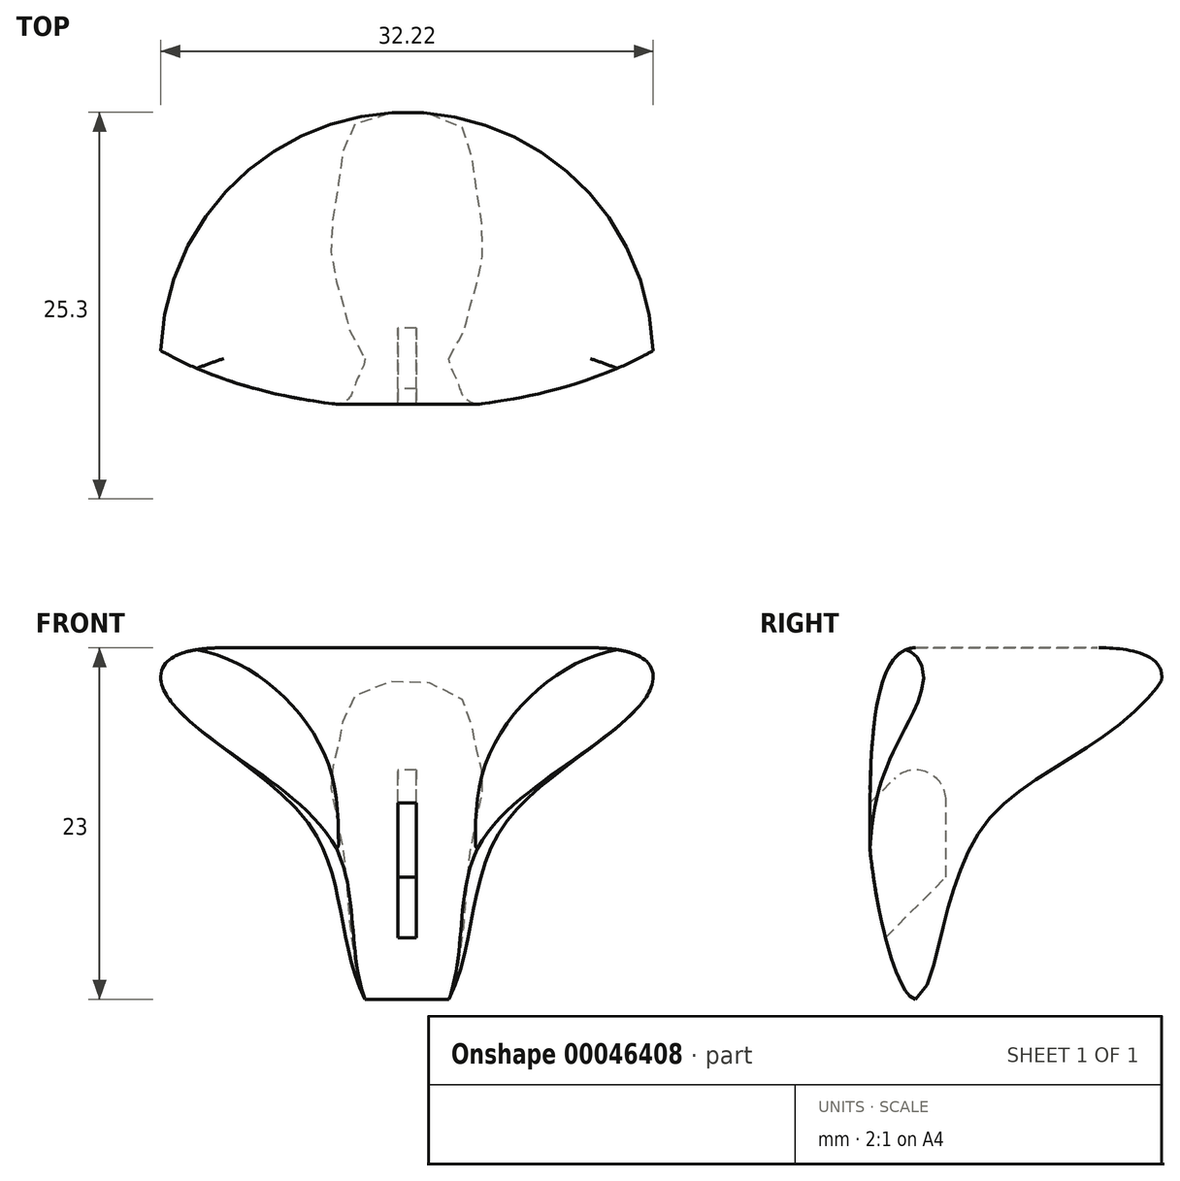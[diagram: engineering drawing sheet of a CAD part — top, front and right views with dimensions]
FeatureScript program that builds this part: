
annotation { "Feature Type Name" : "Feature", "Feature Type Description" : "" }
export const myFeature = defineFeature(function(context is Context, id is Id, definition is map)
    precondition{}
    {
        {
            var Q0;
            Q0=qCreatedBy(makeId("Front.planeOp"),FACE);
            var sketch = newSketch(context, id + "F0", { "sketchPlane" : qUnion([Q0])});
            skLineSegment(sketch, "E0", {"start": v(0, 15) * mm, "end": v(12, 15) * mm});
            skFitSpline(sketch, "E1", {"points": [v(12, 15) * mm, v(15.8, 12) * mm, v(7, 4.23) * mm, v(4, -3.98) * mm, v(0, -10) * mm], "startDerivative": vector(61.5, 0) * mm, "endDerivative": vector(-31.43, 0) * mm});
            skFitSpline(sketch, "E2.MirrorCS", {"points": [v(-12, 15) * mm, v(-15.8, 12) * mm, v(-7, 4.23) * mm, v(-4, -3.98) * mm, v(0, -10) * mm], "startDerivative": vector(-61.5, 0) * mm, "endDerivative": vector(31.43, 0) * mm});
            skLineSegment(sketch, "E3.MirrorCS", {"start": v(0, 15) * mm, "end": v(-12, 15) * mm});
            skLineSegment(sketch, "E4", {"start": v(0, 15) * mm, "end": v(0, -10) * mm});
            skSolve(sketch);
        }
        {
            var Q0;
            Q0=qCreatedBy(makeId("Right.planeOp"),FACE);
            var sketch = newSketch(context, id + "F1", { "sketchPlane" : qUnion([Q0])});
            skLineSegment(sketch, "E5", {"start": v(0, 15) * mm, "end": v(15, 15) * mm});
            skFitSpline(sketch, "E6", {"points": [v(15, 15) * mm, v(14.5, 11) * mm, v(5, 4) * mm, v(1.5, -4.5) * mm, v(0, -8) * mm, v(-3, 2) * mm, v(0, 15) * mm], "startDerivative": vector(73.61, 0) * mm, "endDerivative": vector(42.65, 0) * mm});
            skLineSegment(sketch, "E7", {"start": v(0, 15) * mm, "end": v(0, -8) * mm});
            skFitSpline(sketch, "E8", {"points": [v(0, 15) * mm, v(-3, 2) * mm], "startDerivative": vector(-9, 0) * mm, "endDerivative": vector(0, -17.41) * mm});
            skLineSegment(sketch, "E9", {"start": v(-3, 2) * mm, "end": v(-3, -8) * mm});
            skLineSegment(sketch, "E10", {"start": v(-3, -8) * mm, "end": v(0, -8) * mm});
            skSolve(sketch);
        }
        {
            var Q0;
            {var subQ0=sQuery(id+"F1.wireOp",EDGE,"8db3f753-8a20-43be-9b9b-d89ddbdbede4");Q0=makeQuery(id+"F1.imprint","IMPRINT",FACE,{"disambiguationData":[TD([[makeQuery(id+"F1.imprint","IMPRINT",EDGE,{"derivedFrom":subQ0}),-1.0]])]});}
            var Q1;
            {var subQ0=sQuery(id+"F1.wireOp",EDGE,"E5");Q1=makeQuery(id+"F1.imprint","IMPRINT",FACE,{"disambiguationData":[TD([[makeQuery(id+"F1.imprint","IMPRINT",EDGE,{"derivedFrom":subQ0}),-1.0]])]});}
            var Q2;
            Q2=makeQuery(id+"F1.imprint","IMPRINT",FACE,{"disambiguationData":[TD([[makeQuery(id+"F1.imprint","IMPRINT",EDGE,{"derivedFrom":sQuery(id+"F1.wireOp",EDGE,"E7")}),-1.0]])]});
            extrude(context, id + "F2", {"entities" : qUnion([Q0, Q1, Q2]), "depth" : 35 * mm, "offsetDistance" : 25 * mm, "symmetric" : true});
        }
        {
            var Q0;
            Q0=makeQuery(id+"F2.opExtrude","SWEPT_EDGE",EDGE,{"disambiguationData":[OSD([sQuery(id+"F1.wireOp",EDGE,"E9"),sQuery(id+"F1.wireOp",EDGE,"E10")])]});
            fillet(context, id + "F3", {"entities" : qUnion([Q0]), "tangentPropagation" : true, "radius" : 2 * mm, "defaultsChanged" : true, "vertexSettings" : [], "allowEdgeOverflow" : false});
        }
        {
            var Q0;
            Q0=makeQuery(id+"F0.imprint","IMPRINT",FACE,{"disambiguationData":[TD([[makeQuery(id+"F0.imprint","IMPRINT",EDGE,{"derivedFrom":sQuery(id+"F0.wireOp",EDGE,"E0")}),-1.0]])]});
            var Q1;
            Q1=sQuery(id+"F0.wireOp",EDGE,"E4");
            revolve(context, id + "F4", {"surfaceOperationType" : NewSurfaceOperationType.NEW, "entities" : qUnion([Q0]), "axis" : qUnion([Q1]), "revolveType" : RevolveType.FULL});
        }
        {
            var Q0;
            Q0=makeQuery(id+"F4.opRevolve","SWEPT_BODY",BODY,{"disambiguationData":[OSD([sQuery(id+"F0.wireOp",EDGE,"E0"),sQuery(id+"F0.wireOp",EDGE,"E1"),sQuery(id+"F0.wireOp",EDGE,"E4")])]});
            var Q1;
            Q1=makeQuery(id+"F2.opExtrude","SWEPT_BODY",BODY,{"disambiguationData":[OSD([sQuery(id+"F1.wireOp",EDGE,"E6"),sQuery(id+"F1.wireOp",EDGE,"8db3f753-8a20-43be-9b9b-d89ddbdbede4"),sQuery(id+"F1.wireOp",EDGE,"E7")])]});
            booleanBodies(context, id + "F5", {"operationType" : BooleanOperationType.INTERSECTION, "tools" : qUnion([Q0, Q1])});
        }
        {
            var Q0;
            Q0=qCreatedBy(makeId("Right.planeOp"),FACE);
            var sketch = newSketch(context, id + "F6", { "sketchPlane" : qUnion([Q0])});
            skLineSegment(sketch, "E11", {"start": v(-4, -6) * mm, "end": v(2, 0) * mm});
            skLineSegment(sketch, "E12", {"start": v(2, 0) * mm, "end": v(2, 5) * mm});
            skArc(sketch, "E13", {"start": v(2, 5) * mm, "mid": v(0, 7) * mm, "end": v(-2, 5) * mm, "construction": true});
            skLineSegment(sketch, "E14", {"start": v(-4, 3.83) * mm, "end": v(-1.41, 6.41) * mm});
            skArc(sketch, "E15", {"start": v(2, 5) * mm, "mid": v(0.77, 6.85) * mm, "end": v(-1.41, 6.41) * mm});
            skLineSegment(sketch, "E16", {"start": v(-4, 3.83) * mm, "end": v(-4, -6) * mm});
            skSolve(sketch);
        }
        {
            var Q0;
            Q0=makeQuery(id+"F6.imprint","IMPRINT",FACE,{"disambiguationData":[TD([[makeQuery(id+"F6.imprint","IMPRINT",EDGE,{"derivedFrom":sQuery(id+"F6.wireOp",EDGE,"kYgipzbn-bHnc-i11i-ac2v-ZPtl71UpZP5C.bottom")}),-1.0]])]});
            var Q1;
            Q1=makeQuery(id+"F6.imprint","IMPRINT",FACE,{"disambiguationData":[TD([[makeQuery(id+"F6.imprint","IMPRINT",EDGE,{"derivedFrom":sQuery(id+"F6.wireOp",EDGE,"E11")}),1.0]])]});
            extrude(context, id + "F7", {"entities" : qUnion([Q0, Q1]), "operationType" : NewBodyOperationType.REMOVE, "depth" : 1.2 * mm, "offsetDistance" : 25 * mm, "symmetric" : true});
        }
        {
            var Q0;
            Q0=qCreatedBy(makeId("Top.planeOp"),FACE);
            var sketch = newSketch(context, id + "F8", { "sketchPlane" : qUnion([Q0])});
            skEllipse(sketch, "E17", {"center": v(0, 9.25) * mm, "majorRadius": 22.5 * mm, "minorRadius": 12.5 * mm, "majorAxis": v(1, 0)});
            skSolve(sketch);
        }
        {
            var Q0;
            Q0=makeQuery(id+"F8.imprint","IMPRINT",FACE,{"disambiguationData":[TD([[makeQuery(id+"F8.imprint","IMPRINT",EDGE,{"derivedFrom":sQuery(id+"F8.wireOp",EDGE,"E17")}),1.0]])]});
            extrude(context, id + "F9", {"entities" : qUnion([Q0]), "depth" : 20 * mm, "offsetDistance" : 25 * mm, "hasSecondDirection" : true, "secondDirectionOppositeDirection" : true, "secondDirectionDepth" : 10 * mm});
        }
        {
            var Q0;
            Q0=makeQuery(id+"F5.opBoolean","INTERSECT",BODY,{"derivedFrom":[makeQuery(id+"F2.opExtrude","SWEPT_BODY",BODY,{"disambiguationData":[OSD([sQuery(id+"F1.wireOp",EDGE,"E5"),sQuery(id+"F1.wireOp",EDGE,"E6"),sQuery(id+"F1.wireOp",EDGE,"8db3f753-8a20-43be-9b9b-d89ddbdbede4")])]}),makeQuery(id+"F4.opRevolve","SWEPT_BODY",BODY,{"disambiguationData":[OSD([sQuery(id+"F0.wireOp",EDGE,"E0"),sQuery(id+"F0.wireOp",EDGE,"E1"),sQuery(id+"F0.wireOp",EDGE,"E4")])]})]});
            var Q1;
            Q1=makeQuery(id+"F9.opExtrude","SWEPT_BODY",BODY,{"disambiguationData":[OSD([sQuery(id+"F8.wireOp",EDGE,"E17")])]});
            booleanBodies(context, id + "F10", {"operationType" : BooleanOperationType.INTERSECTION, "tools" : qUnion([Q0, Q1])});
        }
    });
